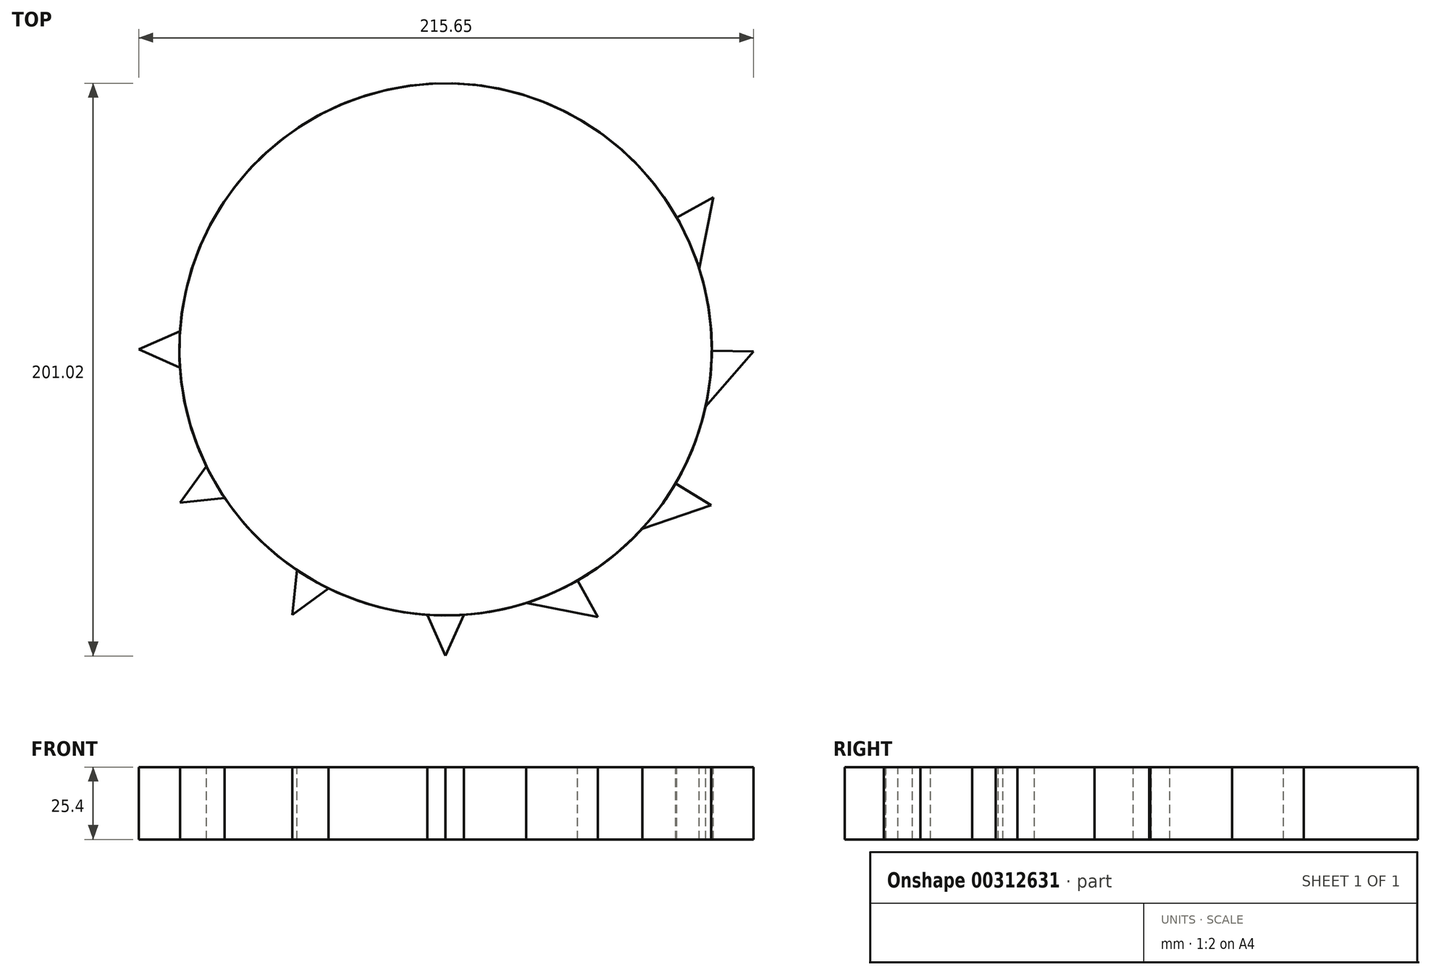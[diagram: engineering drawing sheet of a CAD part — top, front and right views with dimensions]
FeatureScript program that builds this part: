
annotation { "Feature Type Name" : "Feature", "Feature Type Description" : "" }
export const myFeature = defineFeature(function(context is Context, id is Id, definition is map)
    precondition{}
    {
        {
            var Q0;
            Q0=qCreatedBy(makeId("Top.planeOp"),FACE);
            var sketch = newSketch(context, id + "F0", { "sketchPlane" : qUnion([Q0])});
            skCircle(sketch, "E0", {"center": v(0, 0) * mm, "radius": 93.4 * mm});
            skSolve(sketch);
        }
        {
            var Q0;
            Q0 = qSketchRegion(id + "F0", true);
            extrude(context, id + "F1", {"entities" : qUnion([Q0]), "depth" : 25.4 * mm});
        }
        {
            var Q0;
            Q0=makeQuery(id+"F1.opExtrude","CAP_FACE",FACE,{"disambiguationData":[OSD([sQuery(id+"F0.wireOp",EDGE,"E0")])],"isStart":false});
            var sketch = newSketch(context, id + "F2", { "sketchPlane" : qUnion([Q0])});
            skLineSegment(sketch, "E1", {"start": v(81.12, 46.31) * mm, "end": v(93.94, 53.37) * mm});
            skLineSegment(sketch, "E2", {"start": v(93.94, 53.37) * mm, "end": v(89.01, 28.32) * mm});
            skLineSegment(sketch, "E3", {"start": v(0, -107.6) * mm, "end": v(6.42, -93.19) * mm});
            skLineSegment(sketch, "E4.MirrorCS", {"start": v(0, -107.6) * mm, "end": v(-6.42, -93.19) * mm});
            skSolve(sketch);
        }
        {
            var Q0;
            {var subQ0=sQuery(id+"F2.wireOp",EDGE,"E3");Q0=makeQuery(id+"F2.imprint","IMPRINT",FACE,{"disambiguationData":[TD([[makeQuery(id+"F2.imprint","IMPRINT",EDGE,{"derivedFrom":subQ0}),1.0]])]});}
            extrude(context, id + "F3", {"entities" : qUnion([Q0]), "operationType" : NewBodyOperationType.ADD, "oppositeDirection" : true, "depth" : 25.4 * mm});
        }
        {
            var Q0;
            {var subQ0=sQuery(id+"F2.wireOp",EDGE,"E1");Q0=makeQuery(id+"F2.imprint","IMPRINT",FACE,{"disambiguationData":[TD([[makeQuery(id+"F2.imprint","IMPRINT",EDGE,{"derivedFrom":subQ0}),-1.0]])]});}
            extrude(context, id + "F4", {"entities" : qUnion([Q0]), "operationType" : NewBodyOperationType.ADD, "oppositeDirection" : true, "depth" : 25.4 * mm});
        }
        {
            var Q0;
            Q0=makeQuery(id+"F1.opExtrude","SWEPT_BODY",BODY,{"disambiguationData":[OSD([sQuery(id+"F0.wireOp",EDGE,"E0")])]});
            var Q1;
            {var subQ1=sQuery(id+"F2.wireOp",EDGE,"E3");var subQ2=sQuery(id+"F0.wireOp",EDGE,"E0");Q1=makeQuery(id+"F4.boolean.opBoolean","SPLIT",FACE,{"disambiguationData":[TD([makeQuery(id+"F3.opExtrude","SWEPT_FACE",FACE,{"disambiguationData":[OSD([subQ1])]})])],"derivedFrom":makeQuery(id+"F1.opExtrude","SWEPT_FACE",FACE,{"disambiguationData":[OSD([subQ2])]})});}
            circularPattern(context, id + "F5", {"entities" : qUnion([Q0]), "axis" : qUnion([Q1]), "angle" : 90 * degree, "instanceCount" : 4, "equalSpace" : true});
        }
    });
